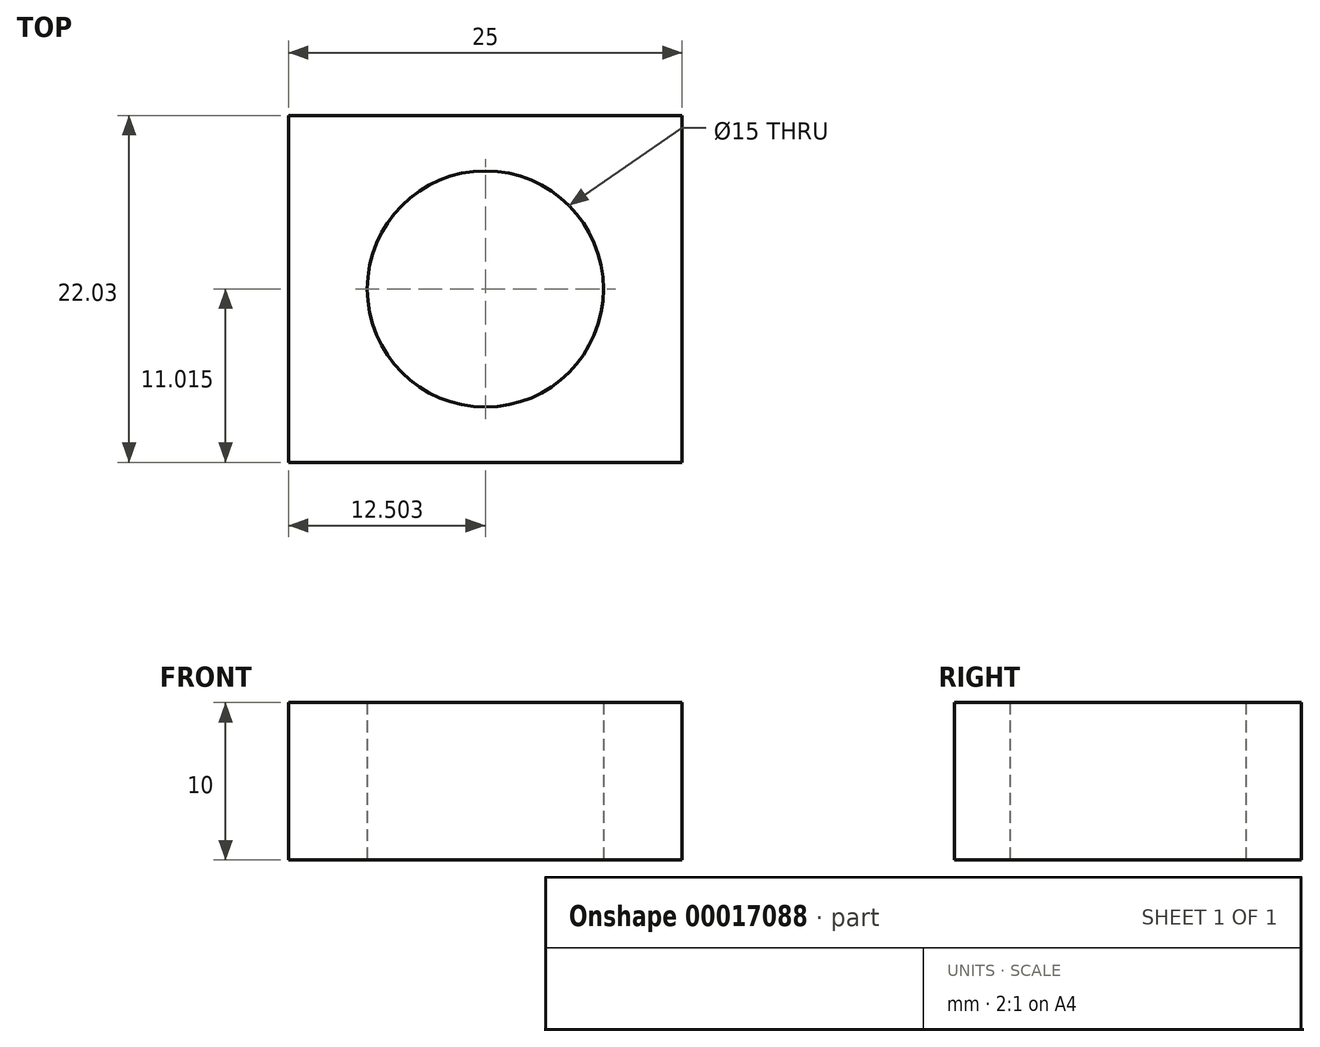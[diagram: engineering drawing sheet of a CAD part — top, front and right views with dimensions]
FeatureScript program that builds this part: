
annotation { "Feature Type Name" : "Feature", "Feature Type Description" : "" }
export const myFeature = defineFeature(function(context is Context, id is Id, definition is map)
    precondition{}
    {
        {
            var Q0;
            Q0=qCreatedBy(makeId("Top.planeOp"),FACE);
            var sketch = newSketch(context, id + "F0", { "sketchPlane" : qUnion([Q0])});
            skLineSegment(sketch, "E0.bottom", {"start": v(-17.17, 12.5) * mm, "end": v(7.83, 12.5) * mm});
            skLineSegment(sketch, "E0.top", {"start": v(-17.17, -9.53) * mm, "end": v(7.83, -9.53) * mm});
            skLineSegment(sketch, "E0.left", {"start": v(-17.17, 12.5) * mm, "end": v(-17.17, -9.53) * mm});
            skLineSegment(sketch, "E0.right", {"start": v(7.83, 12.5) * mm, "end": v(7.83, -9.53) * mm});
            skCircle(sketch, "E1", {"center": v(-4.67, 1.49) * mm, "radius": 7.5 * mm});
            skSolve(sketch);
        }
        {
            var Q0;
            Q0 = qSketchRegion(id + "F0", true);
            var Q1;
            Q1=makeQuery(id+"F0.imprint","IMPRINT",FACE,{"disambiguationData":[TD([[makeQuery(id+"F0.imprint","IMPRINT",EDGE,{"derivedFrom":sQuery(id+"F0.wireOp",EDGE,"E0.bottom")}),-1.0]])]});
            extrude(context, id + "F1", {"entities" : qUnion([Q0, Q1]), "depth" : 10 * mm});
        }
    });
